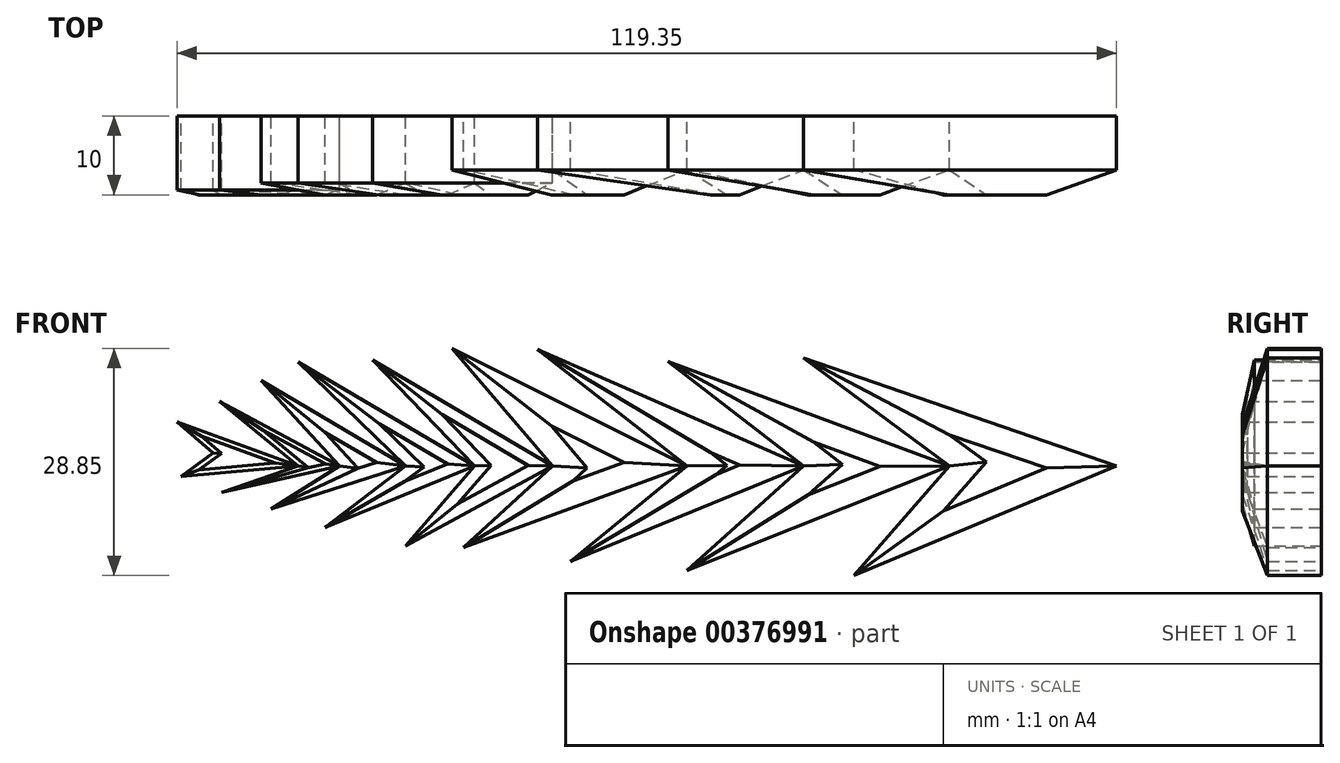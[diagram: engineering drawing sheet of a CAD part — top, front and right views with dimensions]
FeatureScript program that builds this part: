
annotation { "Feature Type Name" : "Feature", "Feature Type Description" : "" }
export const myFeature = defineFeature(function(context is Context, id is Id, definition is map)
    precondition{}
    {
        {
            var Q0;
            Q0=qCreatedBy(makeId("Front.planeOp"),FACE);
            var sketch = newSketch(context, id + "F0", { "sketchPlane" : qUnion([Q0])});
            skLineSegment(sketch, "E0", {"start": v(-64.8, 51.9) * mm, "end": v(-60.17, 47.96) * mm});
            skLineSegment(sketch, "E1", {"start": v(-60.17, 47.96) * mm, "end": v(-64.26, 44.98) * mm});
            skLineSegment(sketch, "E2", {"start": v(-64.26, 44.98) * mm, "end": v(-49.4, 46.33) * mm});
            skLineSegment(sketch, "E3", {"start": v(-49.4, 46.33) * mm, "end": v(-64.8, 51.9) * mm});
            skLineSegment(sketch, "E4", {"start": v(-49.4, 46.33) * mm, "end": v(-59.38, 54.52) * mm});
            skLineSegment(sketch, "E5", {"start": v(-59.38, 54.52) * mm, "end": v(-44.13, 46.33) * mm});
            skLineSegment(sketch, "E6", {"start": v(-44.13, 46.33) * mm, "end": v(-59.12, 42.96) * mm});
            skLineSegment(sketch, "E7", {"start": v(-59.12, 42.96) * mm, "end": v(-49.4, 46.33) * mm});
            skLineSegment(sketch, "E8", {"start": v(-44.13, 46.33) * mm, "end": v(-54.13, 57.15) * mm});
            skLineSegment(sketch, "E9", {"start": v(-54.13, 57.15) * mm, "end": v(-35.74, 46.33) * mm});
            skLineSegment(sketch, "E10", {"start": v(-35.74, 46.33) * mm, "end": v(-52.81, 40.86) * mm});
            skLineSegment(sketch, "E11", {"start": v(-52.81, 40.86) * mm, "end": v(-44.13, 46.33) * mm});
            skLineSegment(sketch, "E12", {"start": v(-35.74, 46.33) * mm, "end": v(-49.4, 59.51) * mm});
            skLineSegment(sketch, "E13", {"start": v(-49.4, 59.51) * mm, "end": v(-26.99, 46.33) * mm});
            skLineSegment(sketch, "E14", {"start": v(-26.99, 46.33) * mm, "end": v(-45.98, 38.5) * mm});
            skLineSegment(sketch, "E15", {"start": v(-45.98, 38.5) * mm, "end": v(-35.74, 46.33) * mm});
            skLineSegment(sketch, "E16", {"start": v(-26.99, 46.33) * mm, "end": v(-39.94, 59.78) * mm});
            skLineSegment(sketch, "E17", {"start": v(-39.94, 59.78) * mm, "end": v(-17.08, 46.33) * mm});
            skLineSegment(sketch, "E18", {"start": v(-17.08, 46.33) * mm, "end": v(-35.74, 36.13) * mm});
            skLineSegment(sketch, "E19", {"start": v(-35.74, 36.13) * mm, "end": v(-26.99, 46.33) * mm});
            skLineSegment(sketch, "E20", {"start": v(-17.08, 46.33) * mm, "end": v(-29.82, 61.26) * mm});
            skLineSegment(sketch, "E21", {"start": v(-29.82, 61.26) * mm, "end": v(0, 46.33) * mm});
            skLineSegment(sketch, "E22", {"start": v(0, 46.33) * mm, "end": v(-28.4, 35.95) * mm});
            skLineSegment(sketch, "E23", {"start": v(-28.4, 35.95) * mm, "end": v(-17.08, 46.33) * mm});
            skLineSegment(sketch, "E24", {"start": v(0, 46.33) * mm, "end": v(-19.02, 61.13) * mm});
            skLineSegment(sketch, "E25", {"start": v(-19.02, 61.13) * mm, "end": v(14.79, 46.33) * mm});
            skLineSegment(sketch, "E26", {"start": v(14.79, 46.33) * mm, "end": v(-14.82, 34.18) * mm});
            skLineSegment(sketch, "E27", {"start": v(-14.82, 34.18) * mm, "end": v(0, 46.33) * mm});
            skLineSegment(sketch, "E28", {"start": v(14.79, 46.33) * mm, "end": v(-2.45, 59.59) * mm});
            skLineSegment(sketch, "E29", {"start": v(-2.45, 59.59) * mm, "end": v(33.35, 46.33) * mm});
            skLineSegment(sketch, "E30", {"start": v(33.35, 46.33) * mm, "end": v(0, 33.07) * mm});
            skLineSegment(sketch, "E31", {"start": v(0, 33.07) * mm, "end": v(14.79, 46.33) * mm});
            skLineSegment(sketch, "E32", {"start": v(33.35, 46.33) * mm, "end": v(14.79, 60.03) * mm});
            skLineSegment(sketch, "E33", {"start": v(14.79, 60.03) * mm, "end": v(54.56, 46.33) * mm});
            skLineSegment(sketch, "E34", {"start": v(54.56, 46.33) * mm, "end": v(21.2, 32.41) * mm});
            skLineSegment(sketch, "E35", {"start": v(21.2, 32.41) * mm, "end": v(33.35, 46.33) * mm});
            skSolve(sketch);
        }
        {
            var Q0;
            Q0 = qSketchRegion(id + "F0", true);
            extrude(context, id + "F1", {"entities" : qUnion([Q0]), "endBound" : BoundingType.SYMMETRIC, "depth" : 10 * mm});
        }
        {
            var Q0;
            Q0=makeQuery(id+"F1.opExtrude","CAP_FACE",FACE,{"disambiguationData":[OSD([sQuery(id+"F0.wireOp",EDGE,"E8"),sQuery(id+"F0.wireOp",EDGE,"E9"),sQuery(id+"F0.wireOp",EDGE,"E10"),sQuery(id+"F0.wireOp",EDGE,"E11")])],"isStart":false});
            var Q1;
            Q1=makeQuery(id+"F1.opExtrude","CAP_FACE",FACE,{"disambiguationData":[OSD([sQuery(id+"F0.wireOp",EDGE,"E16"),sQuery(id+"F0.wireOp",EDGE,"E17"),sQuery(id+"F0.wireOp",EDGE,"E18"),sQuery(id+"F0.wireOp",EDGE,"E19")])],"isStart":false});
            var Q2;
            Q2=makeQuery(id+"F1.opExtrude","CAP_FACE",FACE,{"disambiguationData":[OSD([sQuery(id+"F0.wireOp",EDGE,"E12"),sQuery(id+"F0.wireOp",EDGE,"E13"),sQuery(id+"F0.wireOp",EDGE,"E14"),sQuery(id+"F0.wireOp",EDGE,"E15")])],"isStart":false});
            chamfer(context, id + "F2", {"entities" : qUnion([Q0, Q1, Q2]), "chamferType" : ChamferType.OFFSET_ANGLE, "width" : 1.52 * mm, "oppositeDirection" : false, "angle" : 45 * degree, "tangentPropagation" : true});
        }
        {
            var Q0;
            Q0=makeQuery(id+"F1.opExtrude","CAP_FACE",FACE,{"disambiguationData":[OSD([sQuery(id+"F0.wireOp",EDGE,"E0"),sQuery(id+"F0.wireOp",EDGE,"E1"),sQuery(id+"F0.wireOp",EDGE,"E2"),sQuery(id+"F0.wireOp",EDGE,"E3")])],"isStart":false});
            var Q1;
            Q1=makeQuery(id+"F1.opExtrude","CAP_EDGE",EDGE,{"disambiguationData":[OSD([sQuery(id+"F0.wireOp",EDGE,"E5")])],"isStart":false});
            var Q2;
            Q2=makeQuery(id+"F1.opExtrude","CAP_EDGE",EDGE,{"disambiguationData":[OSD([sQuery(id+"F0.wireOp",EDGE,"E4")])],"isStart":false});
            var Q3;
            Q3=makeQuery(id+"F1.opExtrude","CAP_EDGE",EDGE,{"disambiguationData":[OSD([sQuery(id+"F0.wireOp",EDGE,"E6")])],"isStart":false});
            var Q4;
            Q4=makeQuery(id+"F1.opExtrude","CAP_EDGE",EDGE,{"disambiguationData":[OSD([sQuery(id+"F0.wireOp",EDGE,"E7")])],"isStart":false});
            chamfer(context, id + "F3", {"entities" : qUnion([Q0, Q1, Q2, Q3, Q4]), "width" : 0.64 * mm, "tangentPropagation" : true});
        }
        {
            var Q0;
            Q0=makeQuery(id+"F1.opExtrude","CAP_FACE",FACE,{"disambiguationData":[OSD([sQuery(id+"F0.wireOp",EDGE,"E20"),sQuery(id+"F0.wireOp",EDGE,"E21"),sQuery(id+"F0.wireOp",EDGE,"E22"),sQuery(id+"F0.wireOp",EDGE,"E23")])],"isStart":false});
            var Q1;
            Q1=makeQuery(id+"F1.opExtrude","CAP_FACE",FACE,{"disambiguationData":[OSD([sQuery(id+"F0.wireOp",EDGE,"E24"),sQuery(id+"F0.wireOp",EDGE,"E25"),sQuery(id+"F0.wireOp",EDGE,"E26"),sQuery(id+"F0.wireOp",EDGE,"E27")])],"isStart":false});
            var Q2;
            Q2=makeQuery(id+"F1.opExtrude","CAP_FACE",FACE,{"disambiguationData":[OSD([sQuery(id+"F0.wireOp",EDGE,"E32"),sQuery(id+"F0.wireOp",EDGE,"E33"),sQuery(id+"F0.wireOp",EDGE,"E34"),sQuery(id+"F0.wireOp",EDGE,"E35")])],"isStart":false});
            var Q3;
            Q3=makeQuery(id+"F1.opExtrude","CAP_FACE",FACE,{"disambiguationData":[OSD([sQuery(id+"F0.wireOp",EDGE,"E28"),sQuery(id+"F0.wireOp",EDGE,"E29"),sQuery(id+"F0.wireOp",EDGE,"E30"),sQuery(id+"F0.wireOp",EDGE,"E31")])],"isStart":false});
            chamfer(context, id + "F4", {"entities" : qUnion([Q0, Q1, Q2, Q3]), "chamferType" : ChamferType.OFFSET_ANGLE, "width" : 3.17 * mm, "oppositeDirection" : false, "angle" : 45 * degree, "tangentPropagation" : true});
        }
    });
